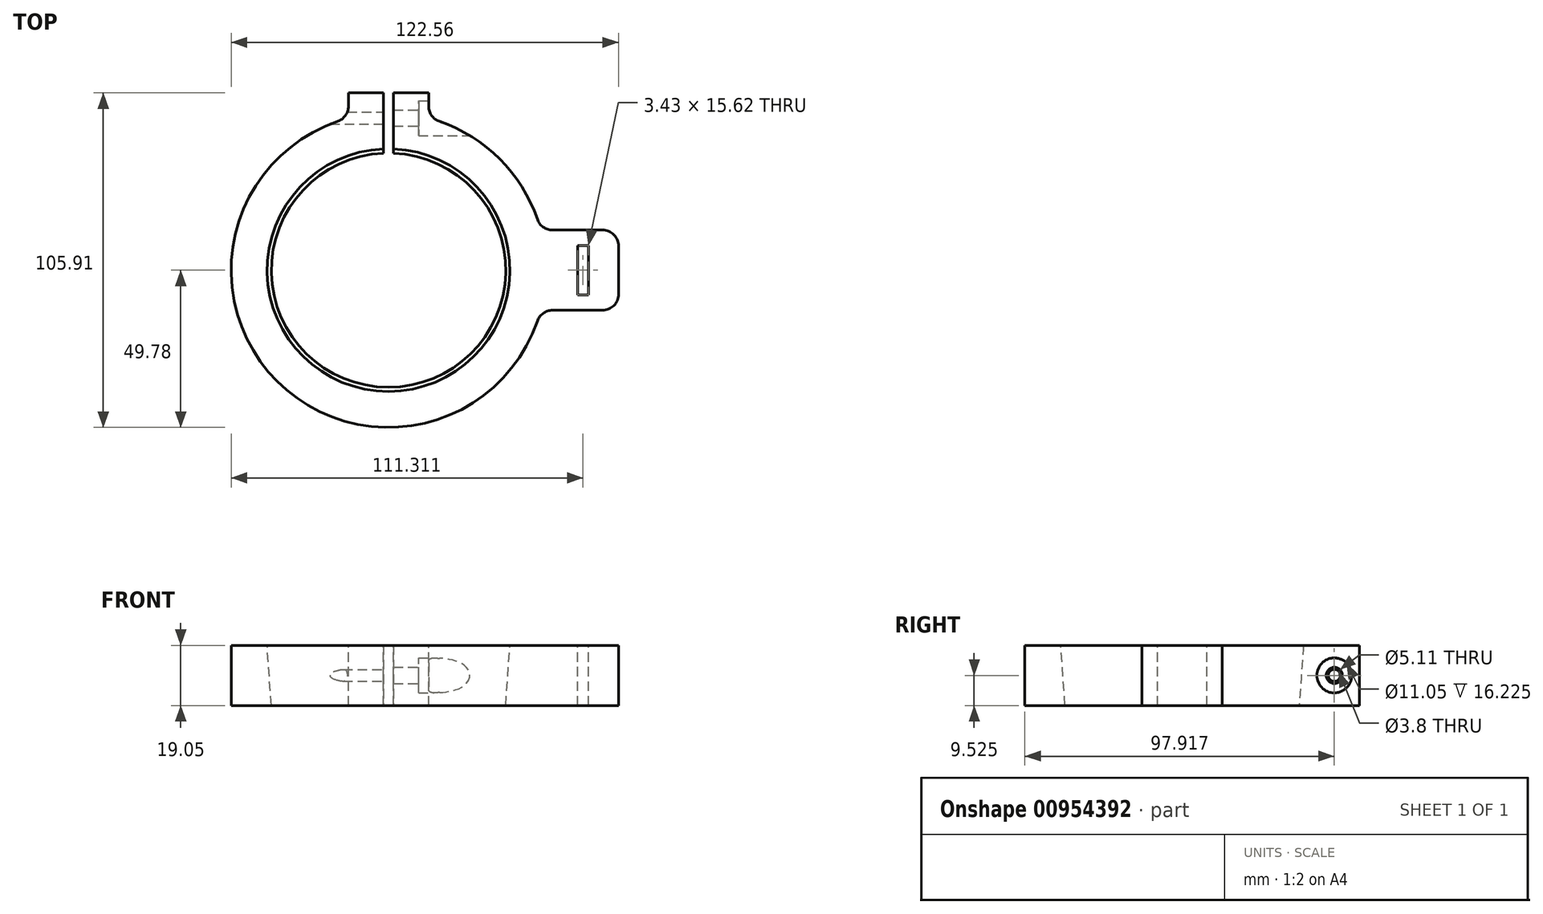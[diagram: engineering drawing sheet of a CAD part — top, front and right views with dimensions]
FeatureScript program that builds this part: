
annotation { "Feature Type Name" : "Feature", "Feature Type Description" : "" }
export const myFeature = defineFeature(function(context is Context, id is Id, definition is map)
    precondition{}
    {
        {
            var Q0;
            Q0=qCreatedBy(makeId("Top.planeOp"),FACE);
            var sketch = newSketch(context, id + "F0", { "sketchPlane" : qUnion([Q0])});
            skCircle(sketch, "E0", {"center": v(0, 0) * mm, "radius": 37.08 * mm});
            skCircle(sketch, "E1", {"center": v(0, 0) * mm, "radius": 49.78 * mm});
            skSolve(sketch);
        }
        {
            var Q0;
            Q0 = qSketchRegion(id + "F0", true);
            extrude(context, id + "F1", {"entities" : qUnion([Q0]), "depth" : 19.05 * mm, "offsetDistance" : 25.4 * mm});
        }
        {
            var Q0;
            Q0=makeQuery(id+"F1.opExtrude","CAP_FACE",FACE,{"disambiguationData":[OSD([sQuery(id+"F0.wireOp",EDGE,"E0"),sQuery(id+"F0.wireOp",EDGE,"E1")])],"isStart":true});
            var sketch = newSketch(context, id + "F2", { "sketchPlane" : qUnion([Q0])});
            skCircle(sketch, "E2", {"center": v(0, 0) * mm, "radius": 37.08 * mm});
            skSolve(sketch);
        }
        {
            var Q0;
            Q0 = qSketchRegion(id + "F2", true);
            extrude(context, id + "F3", {"entities" : qUnion([Q0]), "operationType" : NewBodyOperationType.REMOVE, "oppositeDirection" : true, "depth" : 19.05 * mm, "offsetDistance" : 25.4 * mm, "hasDraft" : true, "draftAngle" : 4 * degree});
        }
        {
            var Q0;
            Q0=makeQuery(id+"F1.opExtrude","CAP_FACE",FACE,{"disambiguationData":[OSD([sQuery(id+"F0.wireOp",EDGE,"E0"),sQuery(id+"F0.wireOp",EDGE,"E1")])],"isStart":false});
            var sketch = newSketch(context, id + "F4", { "sketchPlane" : qUnion([Q0])});
            skLineSegment(sketch, "E3.bottom", {"start": v(-12.7, 56.13) * mm, "end": v(12.7, 56.13) * mm});
            skLineSegment(sketch, "E3.top", {"start": v(-12.7, 38.42) * mm, "end": v(12.7, 38.42) * mm});
            skLineSegment(sketch, "E3.left", {"start": v(-12.7, 56.13) * mm, "end": v(-12.7, 38.42) * mm});
            skLineSegment(sketch, "E3.right", {"start": v(12.7, 56.13) * mm, "end": v(12.7, 38.42) * mm});
            skSolve(sketch);
        }
        {
            var Q0;
            Q0 = qSketchRegion(id + "F4", true);
            extrude(context, id + "F5", {"entities" : qUnion([Q0]), "operationType" : NewBodyOperationType.ADD, "oppositeDirection" : true, "depth" : 19.05 * mm, "offsetDistance" : 25.4 * mm});
        }
        {
            var Q0;
            Q0=makeQuery(id+"F5.boolean.opBoolean","MERGE",FACE,{"derivedFrom":[makeQuery(id+"F1.opExtrude","CAP_FACE",FACE,{"disambiguationData":[OSD([sQuery(id+"F0.wireOp",EDGE,"E0"),sQuery(id+"F0.wireOp",EDGE,"E1")])],"isStart":false}),makeQuery(id+"F5.opExtrude","CAP_FACE",FACE,{"disambiguationData":[OSD([sQuery(id+"F4.wireOp",EDGE,"E3.bottom"),sQuery(id+"F4.wireOp",EDGE,"E3.top"),sQuery(id+"F4.wireOp",EDGE,"E3.left"),sQuery(id+"F4.wireOp",EDGE,"E3.right")])],"isStart":true})]});
            var sketch = newSketch(context, id + "F6", { "sketchPlane" : qUnion([Q0])});
            skLineSegment(sketch, "E4.bottom", {"start": v(-1.59, 56.13) * mm, "end": v(1.59, 56.13) * mm});
            skLineSegment(sketch, "E4.top", {"start": v(-1.59, 37.05) * mm, "end": v(1.59, 37.05) * mm});
            skLineSegment(sketch, "E4.left", {"start": v(-1.59, 56.13) * mm, "end": v(-1.59, 37.05) * mm});
            skLineSegment(sketch, "E4.right", {"start": v(1.59, 56.13) * mm, "end": v(1.59, 37.05) * mm});
            skSolve(sketch);
        }
        {
            var Q0;
            Q0 = qSketchRegion(id + "F6", true);
            extrude(context, id + "F7", {"entities" : qUnion([Q0]), "operationType" : NewBodyOperationType.REMOVE, "endBound" : BoundingType.THROUGH_ALL, "oppositeDirection" : true, "depth" : 25.4 * mm, "offsetDistance" : 25.4 * mm});
        }
        {
            var Q0;
            Q0=makeQuery(id+"F5.boolean.opBoolean","MERGE",FACE,{"derivedFrom":[makeQuery(id+"F1.opExtrude","CAP_FACE",FACE,{"disambiguationData":[OSD([sQuery(id+"F0.wireOp",EDGE,"E0"),sQuery(id+"F0.wireOp",EDGE,"E1")])],"isStart":false}),makeQuery(id+"F5.opExtrude","CAP_FACE",FACE,{"disambiguationData":[OSD([sQuery(id+"F4.wireOp",EDGE,"E3.bottom"),sQuery(id+"F4.wireOp",EDGE,"E3.top"),sQuery(id+"F4.wireOp",EDGE,"E3.left"),sQuery(id+"F4.wireOp",EDGE,"E3.right")])],"isStart":true})]});
            var sketch = newSketch(context, id + "F8", { "sketchPlane" : qUnion([Q0])});
            skLineSegment(sketch, "E5.bottom", {"start": v(38.42, 12.7) * mm, "end": v(72.78, 12.7) * mm});
            skLineSegment(sketch, "E5.top", {"start": v(38.42, -12.7) * mm, "end": v(72.78, -12.7) * mm});
            skLineSegment(sketch, "E5.left", {"start": v(38.42, 12.7) * mm, "end": v(38.42, -12.7) * mm});
            skLineSegment(sketch, "E5.right", {"start": v(72.78, 12.7) * mm, "end": v(72.78, -12.7) * mm});
            skSolve(sketch);
        }
        {
            var Q0;
            Q0 = qSketchRegion(id + "F8", true);
            extrude(context, id + "F9", {"entities" : qUnion([Q0]), "operationType" : NewBodyOperationType.ADD, "oppositeDirection" : true, "depth" : 19.05 * mm, "offsetDistance" : 25.4 * mm});
        }
        {
            var Q0;
            Q0=makeQuery(id+"F9.boolean.opBoolean","MERGE",FACE,{"derivedFrom":[makeQuery(id+"F5.boolean.opBoolean","MERGE",FACE,{"derivedFrom":[makeQuery(id+"F1.opExtrude","CAP_FACE",FACE,{"disambiguationData":[OSD([sQuery(id+"F0.wireOp",EDGE,"E0"),sQuery(id+"F0.wireOp",EDGE,"E1")])],"isStart":false}),makeQuery(id+"F5.opExtrude","CAP_FACE",FACE,{"disambiguationData":[OSD([sQuery(id+"F4.wireOp",EDGE,"E3.bottom"),sQuery(id+"F4.wireOp",EDGE,"E3.top"),sQuery(id+"F4.wireOp",EDGE,"E3.left"),sQuery(id+"F4.wireOp",EDGE,"E3.right")])],"isStart":true})]}),makeQuery(id+"F9.opExtrude","CAP_FACE",FACE,{"disambiguationData":[OSD([sQuery(id+"F8.wireOp",EDGE,"E5.bottom"),sQuery(id+"F8.wireOp",EDGE,"E5.top"),sQuery(id+"F8.wireOp",EDGE,"E5.left"),sQuery(id+"F8.wireOp",EDGE,"E5.right")])],"isStart":true})]});
            var sketch = newSketch(context, id + "F10", { "sketchPlane" : qUnion([Q0])});
            skLineSegment(sketch, "E6.bottom", {"start": v(59.82, 7.81) * mm, "end": v(63.25, 7.81) * mm});
            skLineSegment(sketch, "E6.top", {"start": v(59.82, -7.81) * mm, "end": v(63.25, -7.81) * mm});
            skLineSegment(sketch, "E6.left", {"start": v(59.82, 7.81) * mm, "end": v(59.82, -7.81) * mm});
            skLineSegment(sketch, "E6.right", {"start": v(63.25, 7.81) * mm, "end": v(63.25, -7.81) * mm});
            skSolve(sketch);
        }
        {
            var Q0;
            Q0=makeQuery(id+"F10.imprint","IMPRINT",FACE,{"disambiguationData":[TD([[makeQuery(id+"F10.imprint","IMPRINT",EDGE,{"derivedFrom":sQuery(id+"F10.wireOp",EDGE,"E6.bottom")}),-1.0]])]});
            extrude(context, id + "F11", {"entities" : qUnion([Q0]), "operationType" : NewBodyOperationType.REMOVE, "endBound" : BoundingType.THROUGH_ALL, "oppositeDirection" : true, "depth" : 25.4 * mm, "offsetDistance" : 25.4 * mm});
        }
        {
            var Q0;
            Q0=makeQuery(id+"F5.opExtrude","SWEPT_FACE",FACE,{"disambiguationData":[OSD([sQuery(id+"F4.wireOp",EDGE,"E3.right")])]});
            var sketch = newSketch(context, id + "F12", { "sketchPlane" : qUnion([Q0])});
            skCircle(sketch, "E7", {"center": v(48.14, 9.53) * mm, "radius": 2.55 * mm});
            skSolve(sketch);
        }
        {
            var Q0;
            Q0 = qSketchRegion(id + "F12", true);
            extrude(context, id + "F13", {"entities" : qUnion([Q0]), "operationType" : NewBodyOperationType.REMOVE, "endBound" : BoundingType.UP_TO_NEXT, "oppositeDirection" : true, "depth" : 25.4 * mm, "offsetDistance" : 25.4 * mm, "hasSecondDirection" : true, "secondDirectionBound" : SecondDirectionBoundingType.THROUGH_ALL, "secondDirectionOppositeDirection" : false, "secondDirectionDepth" : 25.4 * mm});
        }
        {
            var Q0;
            Q0=makeQuery(id+"F5.opExtrude","SWEPT_FACE",FACE,{"disambiguationData":[OSD([sQuery(id+"F4.wireOp",EDGE,"E3.right")])]});
            var sketch = newSketch(context, id + "F14", { "sketchPlane" : qUnion([Q0])});
            skCircle(sketch, "E8", {"center": v(48.14, 9.53) * mm, "radius": 5.52 * mm});
            skSolve(sketch);
        }
        {
            var Q0;
            Q0 = qSketchRegion(id + "F14", true);
            extrude(context, id + "F15", {"entities" : qUnion([Q0]), "operationType" : NewBodyOperationType.REMOVE, "oppositeDirection" : true, "depth" : 3.17 * mm, "offsetDistance" : 25.4 * mm, "hasSecondDirection" : true, "secondDirectionBound" : SecondDirectionBoundingType.THROUGH_ALL, "secondDirectionOppositeDirection" : false, "secondDirectionDepth" : 25.4 * mm});
        }
        {
            var Q0;
            Q0=makeQuery(id+"F7.boolean.opBoolean","COPY",FACE,{"derivedFrom":makeQuery(id+"F7.opExtrude","SWEPT_FACE",FACE,{"disambiguationData":[OSD([sQuery(id+"F6.wireOp",EDGE,"E4.left")])]})});
            var sketch = newSketch(context, id + "F16", { "sketchPlane" : qUnion([Q0])});
            skPoint(sketch, "E9", {"position": v(48.14, 9.53) * mm});
            skPoint(sketch, "E10", {"position": v(56.13, 9.53) * mm});
            skSolve(sketch);
        }
        {
            var Q0;
            Q0=sQuery(id+"F16.wireOp",VERTEX,"E9");
            var Q1;
            Q1=makeQuery(id+"F1.opExtrude","SWEPT_BODY",BODY,{"disambiguationData":[OSD([sQuery(id+"F0.wireOp",EDGE,"E0"),sQuery(id+"F0.wireOp",EDGE,"E1")])]});
            hole(context, id + "F17", {"style" : HoleStyle.SIMPLE, "endStyle" : HoleEndStyle.THROUGH, "standardTappedOrClearance" : lookupTablePath({ "standard" : "ANSI", "engagement" : "75%", "pitch" : "24 tpi", "size" : "#10", "type" : "Tapped" }), "standardBlindInLast" : lookupTablePath({ "standard" : "ANSI", "fit" : "Normal", "engagement" : "75%", "pitch" : "24 tpi", "size" : "#10", "type" : "Clearance & tapped" }), "holeDiameter" : 3.8 * mm, "majorDiameter" : 4.83 * mm, "showTappedDepth" : true, "isTappedThrough" : true, "tappedDepth" : 25.43 * mm, "tapClearance" : 3, "locations" : qUnion([Q0]), "scope" : qUnion([Q1])});
        }
        {
            var Q0;
            Q0=makeQuery(id+"F9.boolean.opBoolean","INTERSECT",EDGE,{"derivedFrom":[makeQuery(id+"F1.opExtrude","SWEPT_FACE",FACE,{"disambiguationData":[OSD([sQuery(id+"F0.wireOp",EDGE,"E1")])]}),makeQuery(id+"F9.opExtrude","SWEPT_FACE",FACE,{"disambiguationData":[OSD([sQuery(id+"F8.wireOp",EDGE,"E5.top")])]})]});
            var Q1;
            Q1=makeQuery(id+"F9.opExtrude","SWEPT_EDGE",EDGE,{"disambiguationData":[OSD([sQuery(id+"F8.wireOp",EDGE,"E5.top"),sQuery(id+"F8.wireOp",EDGE,"E5.right")])]});
            var Q2;
            Q2=makeQuery(id+"F9.opExtrude","SWEPT_EDGE",EDGE,{"disambiguationData":[OSD([sQuery(id+"F8.wireOp",EDGE,"E5.bottom"),sQuery(id+"F8.wireOp",EDGE,"E5.right")])]});
            var Q3;
            Q3=makeQuery(id+"F9.boolean.opBoolean","INTERSECT",EDGE,{"derivedFrom":[makeQuery(id+"F1.opExtrude","SWEPT_FACE",FACE,{"disambiguationData":[OSD([sQuery(id+"F0.wireOp",EDGE,"E1")])]}),makeQuery(id+"F9.opExtrude","SWEPT_FACE",FACE,{"disambiguationData":[OSD([sQuery(id+"F8.wireOp",EDGE,"E5.bottom")])]})]});
            var Q4;
            {var subQ0=sQuery(id+"F4.wireOp",EDGE,"E3.right");var subQ1=makeQuery(id+"F5.opExtrude","SWEPT_FACE",FACE,{"disambiguationData":[OSD([subQ0])]});var subQ2=sQuery(id+"F0.wireOp",EDGE,"E1");var subQ3=makeQuery(id+"F1.opExtrude","SWEPT_FACE",FACE,{"disambiguationData":[OSD([subQ2])]});Q4=makeQuery(id+"F13.boolean.opBoolean","SPLIT",EDGE,{"disambiguationData":[TD([makeQuery(id+"F1.opExtrude","CAP_FACE",FACE,{"disambiguationData":[OSD([sQuery(id+"F0.wireOp",EDGE,"E0"),subQ2])],"isStart":true})])],"derivedFrom":makeQuery(id+"F5.boolean.opBoolean","INTERSECT",EDGE,{"derivedFrom":[subQ3,subQ1]})});}
            var Q5;
            {var subQ0=sQuery(id+"F4.wireOp",EDGE,"E3.right");var subQ1=makeQuery(id+"F5.opExtrude","SWEPT_FACE",FACE,{"disambiguationData":[OSD([subQ0])]});var subQ2=sQuery(id+"F0.wireOp",EDGE,"E1");var subQ3=makeQuery(id+"F1.opExtrude","SWEPT_FACE",FACE,{"disambiguationData":[OSD([subQ2])]});Q5=makeQuery(id+"F13.boolean.opBoolean","SPLIT",EDGE,{"disambiguationData":[TD([makeQuery(id+"F1.opExtrude","CAP_FACE",FACE,{"disambiguationData":[OSD([sQuery(id+"F0.wireOp",EDGE,"E0"),subQ2])],"isStart":false})])],"derivedFrom":makeQuery(id+"F5.boolean.opBoolean","INTERSECT",EDGE,{"derivedFrom":[subQ3,subQ1]})});}
            var Q6;
            {var subQ0=sQuery(id+"F4.wireOp",EDGE,"E3.left");var subQ1=makeQuery(id+"F5.opExtrude","SWEPT_FACE",FACE,{"disambiguationData":[OSD([subQ0])]});var subQ2=sQuery(id+"F0.wireOp",EDGE,"E1");var subQ3=makeQuery(id+"F1.opExtrude","SWEPT_FACE",FACE,{"disambiguationData":[OSD([subQ2])]});Q6=makeQuery(id+"F17.hole-0.boolean.opBoolean","SPLIT",EDGE,{"disambiguationData":[TD([makeQuery(id+"F1.opExtrude","CAP_FACE",FACE,{"disambiguationData":[OSD([sQuery(id+"F0.wireOp",EDGE,"E0"),subQ2])],"isStart":false})])],"derivedFrom":makeQuery(id+"F5.boolean.opBoolean","INTERSECT",EDGE,{"derivedFrom":[subQ3,subQ1]})});}
            var Q7;
            {var subQ0=sQuery(id+"F4.wireOp",EDGE,"E3.left");var subQ1=makeQuery(id+"F5.opExtrude","SWEPT_FACE",FACE,{"disambiguationData":[OSD([subQ0])]});var subQ2=sQuery(id+"F0.wireOp",EDGE,"E1");var subQ3=makeQuery(id+"F1.opExtrude","SWEPT_FACE",FACE,{"disambiguationData":[OSD([subQ2])]});Q7=makeQuery(id+"F17.hole-0.boolean.opBoolean","SPLIT",EDGE,{"disambiguationData":[TD([makeQuery(id+"F1.opExtrude","CAP_FACE",FACE,{"disambiguationData":[OSD([sQuery(id+"F0.wireOp",EDGE,"E0"),subQ2])],"isStart":true})])],"derivedFrom":makeQuery(id+"F5.boolean.opBoolean","INTERSECT",EDGE,{"derivedFrom":[subQ3,subQ1]})});}
            fillet(context, id + "F18", {"entities" : qUnion([Q0, Q1, Q2, Q3, Q4, Q5, Q6, Q7]), "radius" : 5.08 * mm, "tangentPropagation" : true, "allowEdgeOverflow" : false});
        }
    });
